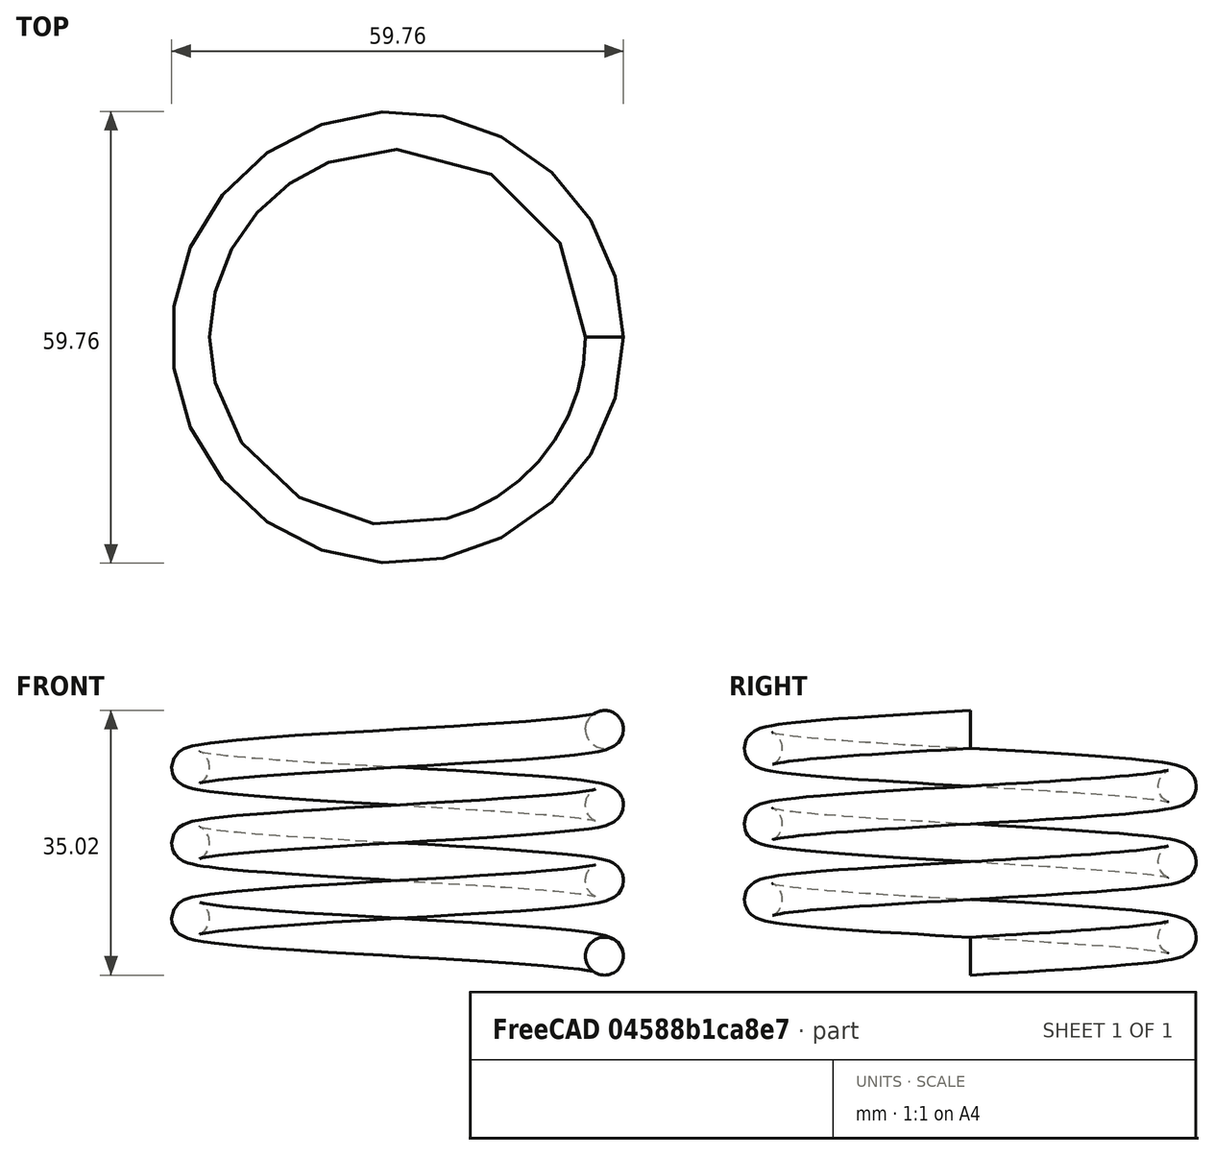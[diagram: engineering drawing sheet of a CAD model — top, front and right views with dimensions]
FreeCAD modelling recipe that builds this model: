
FCSTD DOCUMENT  (FreeCAD 0.21R33771 (Git))
Label: spring
License: All rights reserved
LicenseURL: http://en.wikipedia.org/wiki/All_rights_reserved
objects: Sketcher::SketchObject×1, PartDesign::AdditiveHelix×1, PartDesign::Body×1
note: 4 computed .brp shape members not serialized (recipe doc carries the construction recipe); baked Part::Feature solids carry a one-line shape summary decoded from their .brp

FEATURE [Sketcher::SketchObject] Sketch
  FullyConstrained = false
  MapMode = 5
  Placement = pos=(0,0,0) rot=(1,0,0;1.5708rad)
  Support = -> [XZ_Plane]
  sketch-geometry (1):
    g0: Circle CenterX=27.371 CenterY=0 CenterZ=0 NormalX=0 NormalY=0 NormalZ=1 AngleXU=0 Radius=2.50829
  constraints (1):
    c: PointOnObject(g0,g-1)
FEATURE [PartDesign::AdditiveHelix] AdditiveHelix
  Angle = 0
  Axis = (0,2e-16,1)
  Base = (0,0,0)
  Growth = 0
  HasBeenEdited = true
  Height = 48.41
  LeftHanded = false
  Mode = 0
  Outside = false
  Pitch = 7.80397
  Placement = pos=(0,0,0) rot=(1,0,0;1.5708rad)
  Profile = -> Sketch
  ReferenceAxis = -> Sketch [V_Axis]
  Refine = true
  Turns = 6.20325
FEATURE [PartDesign::Body] Body
  Group = -> [Sketch,AdditiveHelix]
  Origin = -> Origin
  Tip = -> AdditiveHelix
